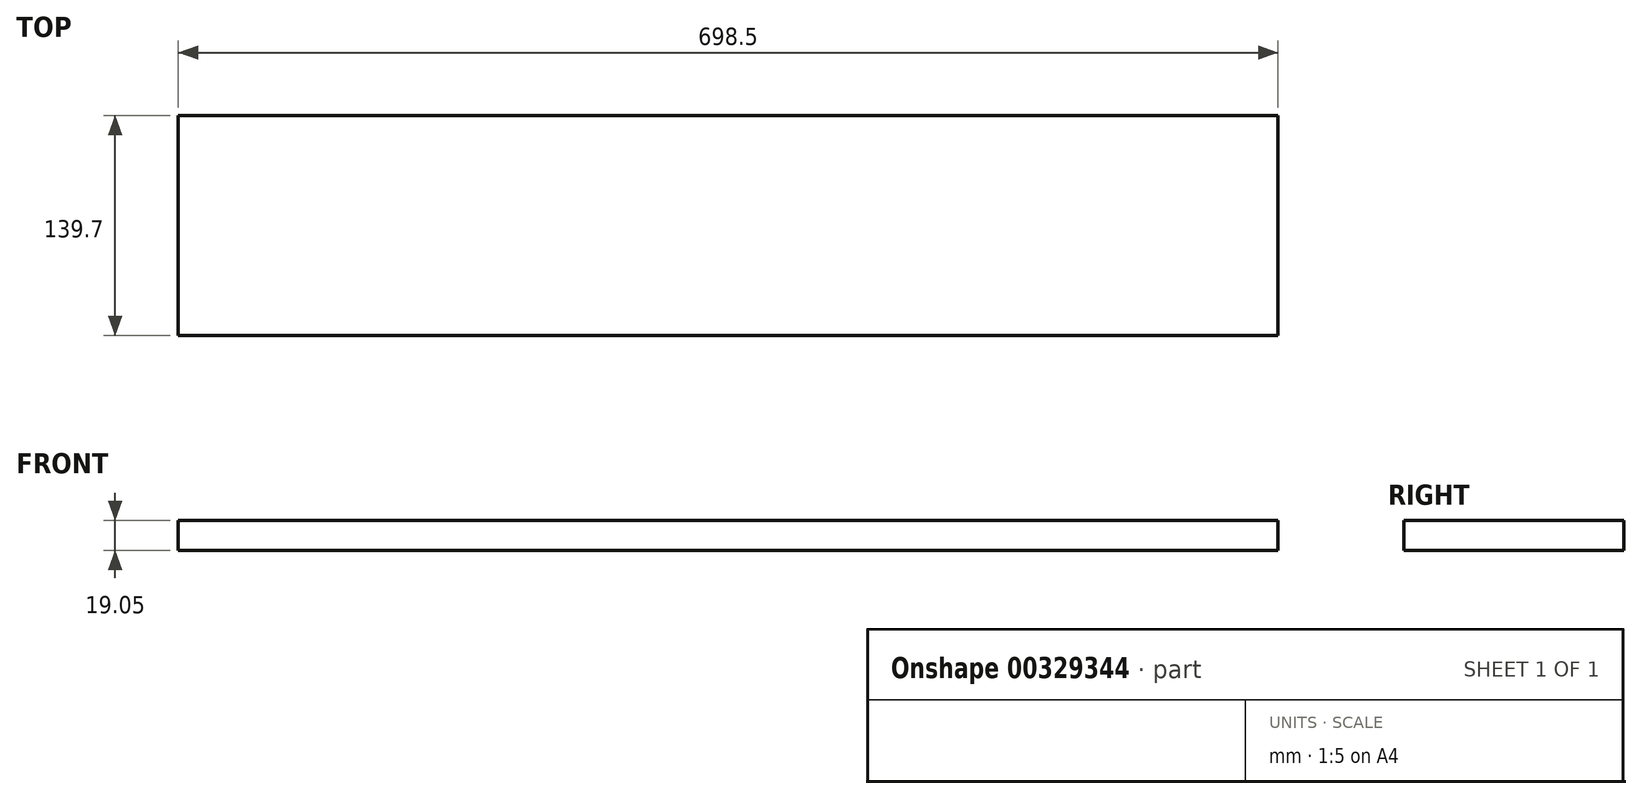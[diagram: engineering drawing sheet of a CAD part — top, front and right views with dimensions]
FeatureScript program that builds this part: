
annotation { "Feature Type Name" : "Feature", "Feature Type Description" : "" }
export const myFeature = defineFeature(function(context is Context, id is Id, definition is map)
    precondition{}
    {
        {
            var Q0;
            Q0=qCreatedBy(makeId("Right.planeOp"),FACE);
            var sketch = newSketch(context, id + "F0", { "sketchPlane" : qUnion([Q0])});
            skLineSegment(sketch, "E0.bottom", {"start": v(0, 0) * mm, "end": v(139.7, 0) * mm});
            skLineSegment(sketch, "E0.top", {"start": v(0, -19.05) * mm, "end": v(139.7, -19.05) * mm});
            skLineSegment(sketch, "E0.left", {"start": v(0, 0) * mm, "end": v(0, -19.05) * mm});
            skLineSegment(sketch, "E0.right", {"start": v(139.7, 0) * mm, "end": v(139.7, -19.05) * mm});
            skSolve(sketch);
        }
        {
            var Q0;
            Q0 = qSketchRegion(id + "F0", true);
            extrude(context, id + "F1", {"entities" : qUnion([Q0]), "depth" : 698.5 * mm});
        }
    });
